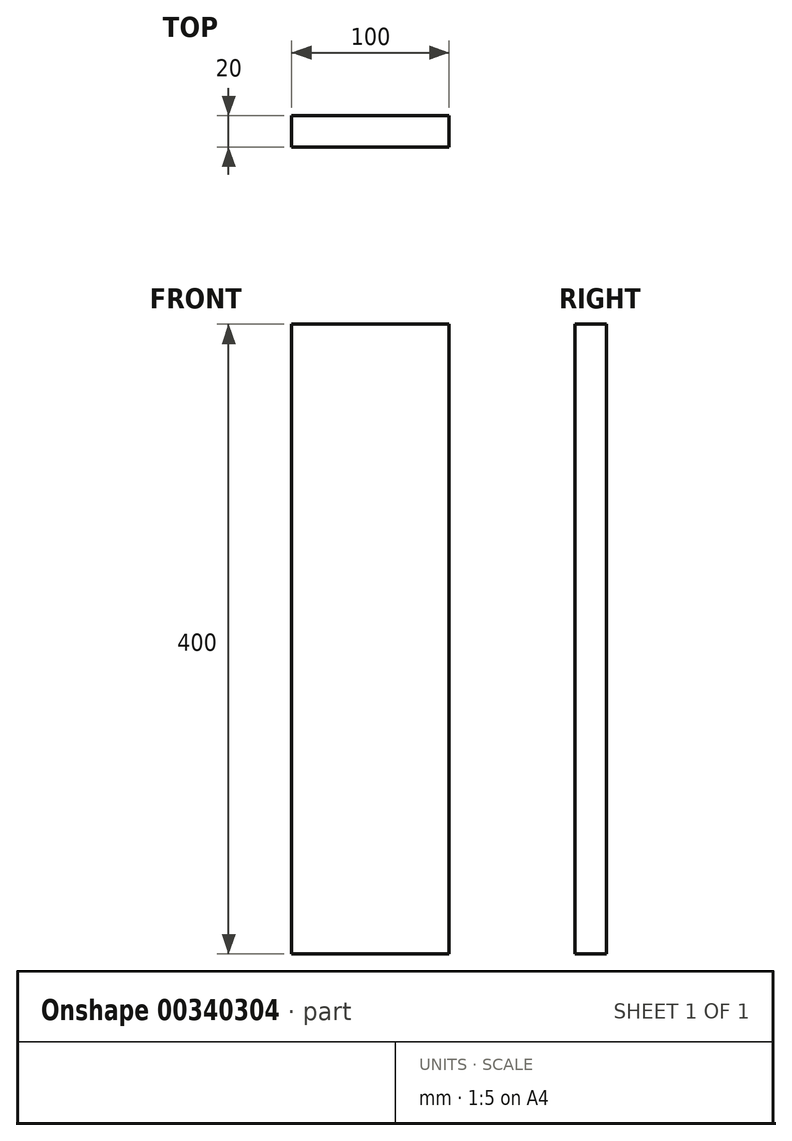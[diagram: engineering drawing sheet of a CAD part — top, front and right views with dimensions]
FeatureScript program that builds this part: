
annotation { "Feature Type Name" : "Feature", "Feature Type Description" : "" }
export const myFeature = defineFeature(function(context is Context, id is Id, definition is map)
    precondition{}
    {
        {
            var Q0;
            Q0=qCreatedBy(makeId("Top.planeOp"),FACE);
            var sketch = newSketch(context, id + "F0", { "sketchPlane" : qUnion([Q0])});
            skLineSegment(sketch, "E0.bottom", {"start": v(50, 10) * mm, "end": v(-50, 10) * mm});
            skLineSegment(sketch, "E0.top", {"start": v(50, -10) * mm, "end": v(-50, -10) * mm});
            skLineSegment(sketch, "E0.left", {"start": v(50, 10) * mm, "end": v(50, -10) * mm});
            skLineSegment(sketch, "E0.right", {"start": v(-50, 10) * mm, "end": v(-50, -10) * mm});
            skPoint(sketch, "E0.middle", {"position": v(0, 0) * mm});
            skSolve(sketch);
        }
        {
            var Q0;
            Q0=makeQuery(id+"F0.imprint","IMPRINT",FACE,{"disambiguationData":[TD([[makeQuery(id+"F0.imprint","IMPRINT",EDGE,{"derivedFrom":sQuery(id+"F0.wireOp",EDGE,"E0.bottom")}),1.0]])]});
            extrude(context, id + "F1", {"entities" : qUnion([Q0]), "depth" : 400 * mm});
        }
    });
